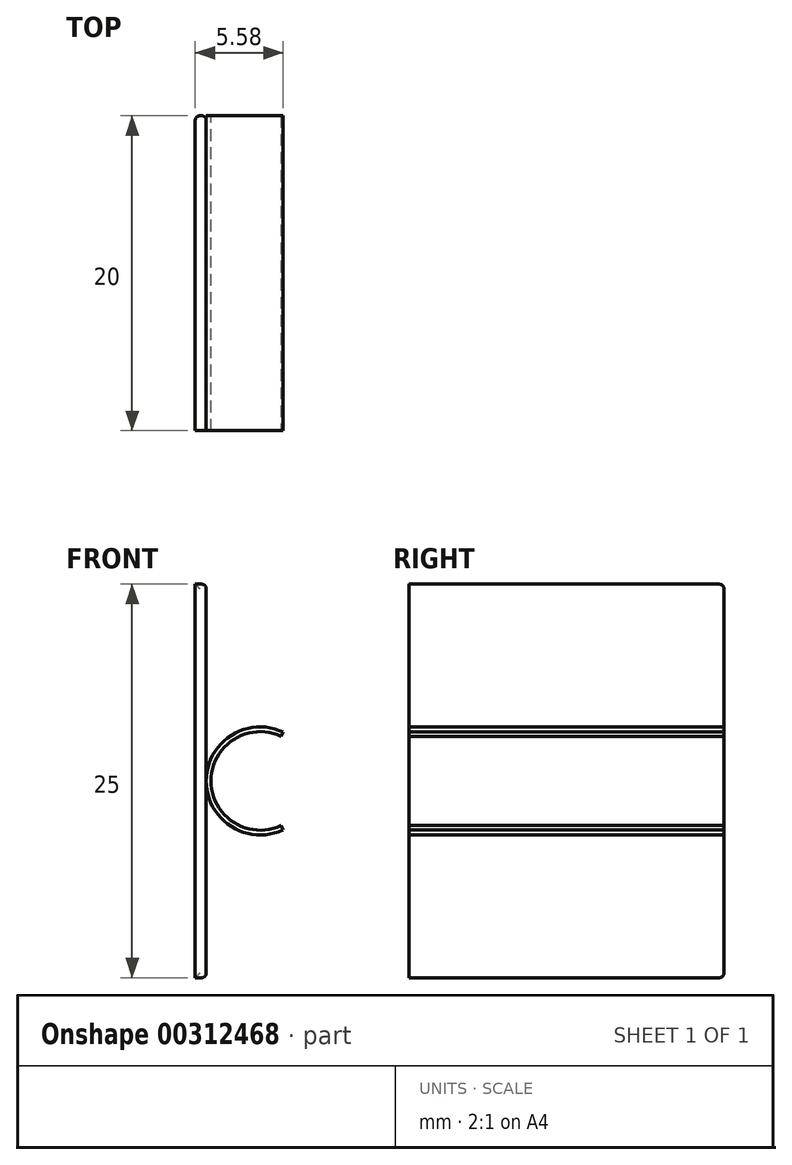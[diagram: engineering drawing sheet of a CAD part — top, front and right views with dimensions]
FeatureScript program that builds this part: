
annotation { "Feature Type Name" : "Feature", "Feature Type Description" : "" }
export const myFeature = defineFeature(function(context is Context, id is Id, definition is map)
    precondition{}
    {
        {
            var Q0;
            Q0=qCreatedBy(makeId("Top.planeOp"),FACE);
            var sketch = newSketch(context, id + "F0", { "sketchPlane" : qUnion([Q0]), "disableImprinting" : false});
            skLineSegment(sketch, "E0.bottom", {"start": v(-9.5, 15) * mm, "end": v(9.5, 15) * mm});
            skLineSegment(sketch, "E0.top", {"start": v(-9.19, -15) * mm, "end": v(-7.4, -15) * mm});
            skLineSegment(sketch, "E0.left", {"start": v(-9.5, 15) * mm, "end": v(-9.5, 13.03) * mm});
            skLineSegment(sketch, "E0.right", {"start": v(9.5, 15) * mm, "end": v(9.5, -15) * mm});
            skPoint(sketch, "E0.middle", {"position": v(0, 0) * mm});
            skLineSegment(sketch, "E1.bottom", {"start": v(-7.6, 13) * mm, "end": v(7.6, 13) * mm});
            skLineSegment(sketch, "E1.right", {"start": v(7.6, 13) * mm, "end": v(7.6, -13) * mm});
            skLineSegment(sketch, "E2", {"start": v(-7.6, 13) * mm, "end": v(-7.4, -4.96) * mm});
            skLineSegment(sketch, "E3", {"start": v(-7.4, -4.96) * mm, "end": v(-7.4, -5.9) * mm});
            skLineSegment(sketch, "E4", {"start": v(7.6, -13) * mm, "end": v(7.6, -15) * mm});
            skLineSegment(sketch, "E5", {"start": v(-9.5, 13.03) * mm, "end": v(-9.19, -15) * mm});
            skLineSegment(sketch, "E6.bottom", {"start": v(8.8, 15) * mm, "end": v(9.8, 15) * mm});
            skLineSegment(sketch, "E6.top", {"start": v(8.8, -5) * mm, "end": v(9.8, -5) * mm});
            skLineSegment(sketch, "E6.left", {"start": v(8.8, 15) * mm, "end": v(8.8, -5) * mm});
            skLineSegment(sketch, "E6.right", {"start": v(9.8, 15) * mm, "end": v(9.8, -5) * mm});
            skLineSegment(sketch, "E7", {"start": v(12.93, 18.21) * mm, "end": v(12.93, -30.13) * mm, "construction": true});
            skArc(sketch, "E8", {"start": v(-7.4, -6.9) * mm, "mid": v(-6.9, -6.4) * mm, "end": v(-7.4, -5.9) * mm});
            skLineSegment(sketch, "E9.trimOffspring", {"start": v(-7.4, -6.9) * mm, "end": v(-7.4, -8.2) * mm});
            skArc(sketch, "E10.1.0.0", {"start": v(-7.4, -9.2) * mm, "mid": v(-6.9, -8.7) * mm, "end": v(-7.4, -8.2) * mm});
            skArc(sketch, "E10.2.0.0", {"start": v(-7.4, -11.5) * mm, "mid": v(-6.9, -11) * mm, "end": v(-7.4, -10.5) * mm});
            skArc(sketch, "E10.3.0.0", {"start": v(-7.4, -13.8) * mm, "mid": v(-6.9, -13.3) * mm, "end": v(-7.4, -12.8) * mm});
            skLineSegment(sketch, "E10.direction1", {"start": v(-7.4, -6.9) * mm, "end": v(-7.4, -8.2) * mm, "construction": true});
            skLineSegment(sketch, "E11.trimOffspring", {"start": v(-7.4, -11.5) * mm, "end": v(-7.4, -12.8) * mm});
            skLineSegment(sketch, "E12.trimOffspring", {"start": v(-7.4, -13.8) * mm, "end": v(-7.4, -15) * mm});
            skLineSegment(sketch, "E13.trimOffspring", {"start": v(-7.4, -9.2) * mm, "end": v(-7.4, -10.5) * mm});
            skLineSegment(sketch, "E14", {"start": v(7.6, -15) * mm, "end": v(7.6, -29.3) * mm});
            skLineSegment(sketch, "E15", {"start": v(7.6, -31.3) * mm, "end": v(7.6, -31.3) * mm});
            skLineSegment(sketch, "E16", {"start": v(7.6, -31.3) * mm, "end": v(9.54, -31.3) * mm});
            skLineSegment(sketch, "E17", {"start": v(9.54, -31.3) * mm, "end": v(9.5, -15) * mm});
            skArc(sketch, "E18", {"start": v(7.6, -29.3) * mm, "mid": v(6.6, -30.35) * mm, "end": v(7.7, -31.3) * mm});
            skSolve(sketch);
        }
        {
            var Q0;
            Q0=makeQuery(id+"F0.imprint","IMPRINT",FACE,{"disambiguationData":[TD([[makeQuery(id+"F0.imprint","IMPRINT",EDGE,{"derivedFrom":sQuery(id+"F0.wireOp",EDGE,"E6.bottom")}),-1.0]])]});
            var Q1;
            Q1=sQuery(id+"F0.wireOp",EDGE,"E7");
            revolve(context, id + "F1", {"surfaceOperationType" : NewSurfaceOperationType.NEW, "entities" : qUnion([Q0]), "thickness" : 5 * mm, "thickness2" : 0 * mm, "thickness1" : 5 * mm, "axis" : qUnion([Q1]), "revolveType" : RevolveType.SYMMETRIC, "angle" : 230 * degree});
        }
        {
            var Q0;
            {var subQ5=sQuery(id+"F0.wireOp",EDGE,"E6.left");Q0=makeQuery(id+"F0.imprint","IMPRINT",FACE,{"disambiguationData":[TD([[makeQuery(id+"F0.imprint","IMPRINT",EDGE,{"derivedFrom":subQ5}),1.0]])]});}
            var Q1;
            Q1=makeQuery(id+"F0.imprint","IMPRINT",FACE,{"disambiguationData":[TD([[makeQuery(id+"F0.imprint","IMPRINT",EDGE,{"derivedFrom":sQuery(id+"F0.wireOp",EDGE,"E0.bottom")}),-1.0]])]});
            extrude(context, id + "F2", {"entities" : qUnion([Q0, Q1]), "operationType" : NewBodyOperationType.ADD, "depth" : 25 * mm, "offsetDistance" : 25 * mm, "symmetric" : true});
        }
        {
            var Q0;
            {var subQ0=sQuery(id+"F0.wireOp",EDGE,"E6.bottom");Q0=makeQuery(id+"F2.boolean.opBoolean","MERGE",FACE,{"derivedFrom":[makeQuery(id+"F1.opRevolve","SWEPT_FACE",FACE,{"disambiguationData":[OSD([subQ0])]}),makeQuery(id+"F2.opExtrude","SWEPT_FACE",FACE,{"disambiguationData":[OSD([sQuery(id+"F0.wireOp",EDGE,"E0.bottom"),subQ0])]})]});}
            var sketch = newSketch(context, id + "F3", { "sketchPlane" : qUnion([Q0]), "disableImprinting" : false});
            skLineSegment(sketch, "E19.bottom", {"start": v(-5.75, -4.6) * mm, "end": v(5.75, -4.6) * mm});
            skLineSegment(sketch, "E19.top", {"start": v(-5.75, 4.6) * mm, "end": v(5.75, 4.6) * mm});
            skLineSegment(sketch, "E19.right", {"start": v(5.75, -4.6) * mm, "end": v(5.75, 4.6) * mm});
            skPoint(sketch, "E19.middle", {"position": v(0, 0) * mm});
            skLineSegment(sketch, "E20", {"start": v(-5.75, -4.6) * mm, "end": v(-2.27, 0) * mm});
            skLineSegment(sketch, "E21", {"start": v(-2.27, 0) * mm, "end": v(-5.75, 4.6) * mm});
            skSolve(sketch);
        }
        {
            var Q0;
            Q0 = qSketchRegion(id + "F3", true);
            extrude(context, id + "F4", {"entities" : qUnion([Q0]), "operationType" : NewBodyOperationType.REMOVE, "endBound" : BoundingType.THROUGH_ALL, "oppositeDirection" : true, "depth" : 25 * mm, "offsetDistance" : 25 * mm});
        }
        {
            var Q0;
            {var subQ0=sQuery(id+"F0.wireOp",EDGE,"E6.bottom");Q0=makeQuery(id+"F2.boolean.opBoolean","MERGE",FACE,{"derivedFrom":[makeQuery(id+"F1.opRevolve","SWEPT_FACE",FACE,{"disambiguationData":[OSD([subQ0])]}),makeQuery(id+"F2.opExtrude","SWEPT_FACE",FACE,{"disambiguationData":[OSD([sQuery(id+"F0.wireOp",EDGE,"E0.bottom"),subQ0])]})]});}
            var Q1;
            Q1=makeQuery(id+"F2.opExtrude","CAP_EDGE",EDGE,{"disambiguationData":[OSD([sQuery(id+"F0.wireOp",EDGE,"E0.right")])],"isStart":false});
            var Q2;
            Q2=makeQuery(id+"F2.opExtrude","CAP_EDGE",EDGE,{"disambiguationData":[OSD([sQuery(id+"F0.wireOp",EDGE,"E5")])],"isStart":false});
            var Q3;
            Q3=makeQuery(id+"F2.opExtrude","SWEPT_FACE",FACE,{"disambiguationData":[OSD([sQuery(id+"F0.wireOp",EDGE,"E0.top")])]});
            var Q4;
            Q4=makeQuery(id+"F2.opExtrude","CAP_EDGE",EDGE,{"disambiguationData":[OSD([sQuery(id+"F0.wireOp",EDGE,"E5")])],"isStart":true});
            var Q5;
            Q5=makeQuery(id+"F2.opExtrude","CAP_EDGE",EDGE,{"disambiguationData":[OSD([sQuery(id+"F0.wireOp",EDGE,"E0.right")])],"isStart":true});
            var Q6;
            Q6=makeQuery(id+"F2.opExtrude","SWEPT_EDGE",EDGE,{"disambiguationData":[OSD([sQuery(id+"F0.wireOp",EDGE,"E16"),sQuery(id+"F0.wireOp",EDGE,"E17")])]});
            var Q7;
            Q7=makeQuery(id+"F1.opRevolve","CAP_EDGE",EDGE,{"disambiguationData":[OSD([sQuery(id+"F0.wireOp",EDGE,"E6.left")])],"isStart":false});
            var Q8;
            Q8=makeQuery(id+"F1.opRevolve","CAP_EDGE",EDGE,{"disambiguationData":[OSD([sQuery(id+"F0.wireOp",EDGE,"E6.right")])],"isStart":false});
            var Q9;
            Q9=makeQuery(id+"F1.opRevolve","CAP_EDGE",EDGE,{"disambiguationData":[OSD([sQuery(id+"F0.wireOp",EDGE,"E6.right")])],"isStart":true});
            var Q10;
            Q10=makeQuery(id+"F1.opRevolve","CAP_EDGE",EDGE,{"disambiguationData":[OSD([sQuery(id+"F0.wireOp",EDGE,"E6.left")])],"isStart":true});
            fillet(context, id + "F5", {"entities" : qUnion([Q0, Q1, Q2, Q3, Q4, Q5, Q6, Q7, Q8, Q9, Q10]), "radius" : 0.3 * mm, "tangentPropagation" : true, "allowEdgeOverflow" : false});
        }
    });
